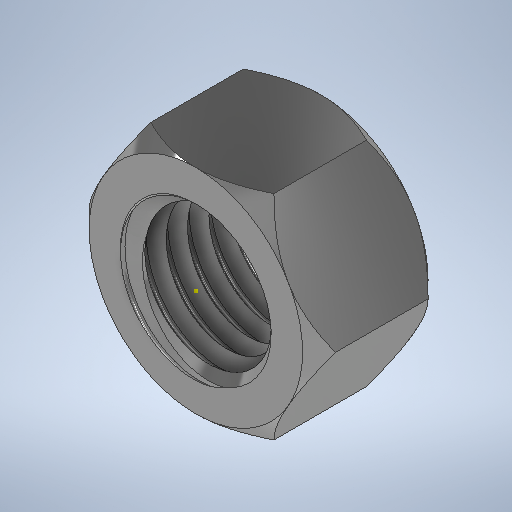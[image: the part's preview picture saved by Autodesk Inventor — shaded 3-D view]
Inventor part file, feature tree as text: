
AUTODESK INVENTOR PART (.ipt)
format: ipt  version: 2025.2 (Build 292293000, 293)  size: 475,136 bytes
history: native  units: in
note: dims shown in document units (in); Inventor stores cm internally (conversion verified against a paired STEP export)
features: sketch x6, extrude x4, chamfer x2, helix x1
ambient origin geometry x8: Origin, YZ Plane, XZ Plane, XY Plane, X Axis, Y Axis, Z Axis, Center Point
bodies: Solid1 (feature_tree)
feature tree (13):
  extrude  "Extrusion1"  Depth=0.3937in TaperAngle=0.0deg
  extrude  "Extrusion2"  Depth=0.6693in
  extrude  "Extrusion3"  Depth=0.3937in
  extrude  "Extrusion4"  Depth=0.0394in TaperAngle=45.0deg
  chamfer  "Chamfer1"  Distance=0.0394in Angle=45.0deg
  chamfer  "Chamfer2"  Distance=0.0787in
  helix  "Coil1"  [1 undecoded]
  sketch  "Sketch6"  dims[d18=60.0deg d19=0.0787in d20=0.1969in d21=0.0079in d22=0.0669in d23=0.5512in d24=0.3937in d25=0.0in d26=90.0deg d27=90.0deg d28=0.0in d29=0.0in]
  sketch  "Sketch1"  dims[d0=0.6693in d1=0.3937in d2=0.0in]
  sketch  "Sketch2"  dims[d3=0.0in d4=45.0deg d5=0.6693in]
  sketch  "Sketch3"  dims[d6=0.0in d7=45.0deg d8=0.3937in]
  sketch  "Sketch4"  dims[d9=0.0in d10=0.0in d11=0.0394in d12=0.0787in d13=45.0deg d14=0.0394in d15=0.0787in d16=45.0deg]
  sketch  "Sketch5"  dims[d17=0.0669in]
note: 1 required parameter value undecoded (feature->parameter linkage not recoverable at this tier; creation-order binding heuristic only, values carry confidence <= 0.55)
